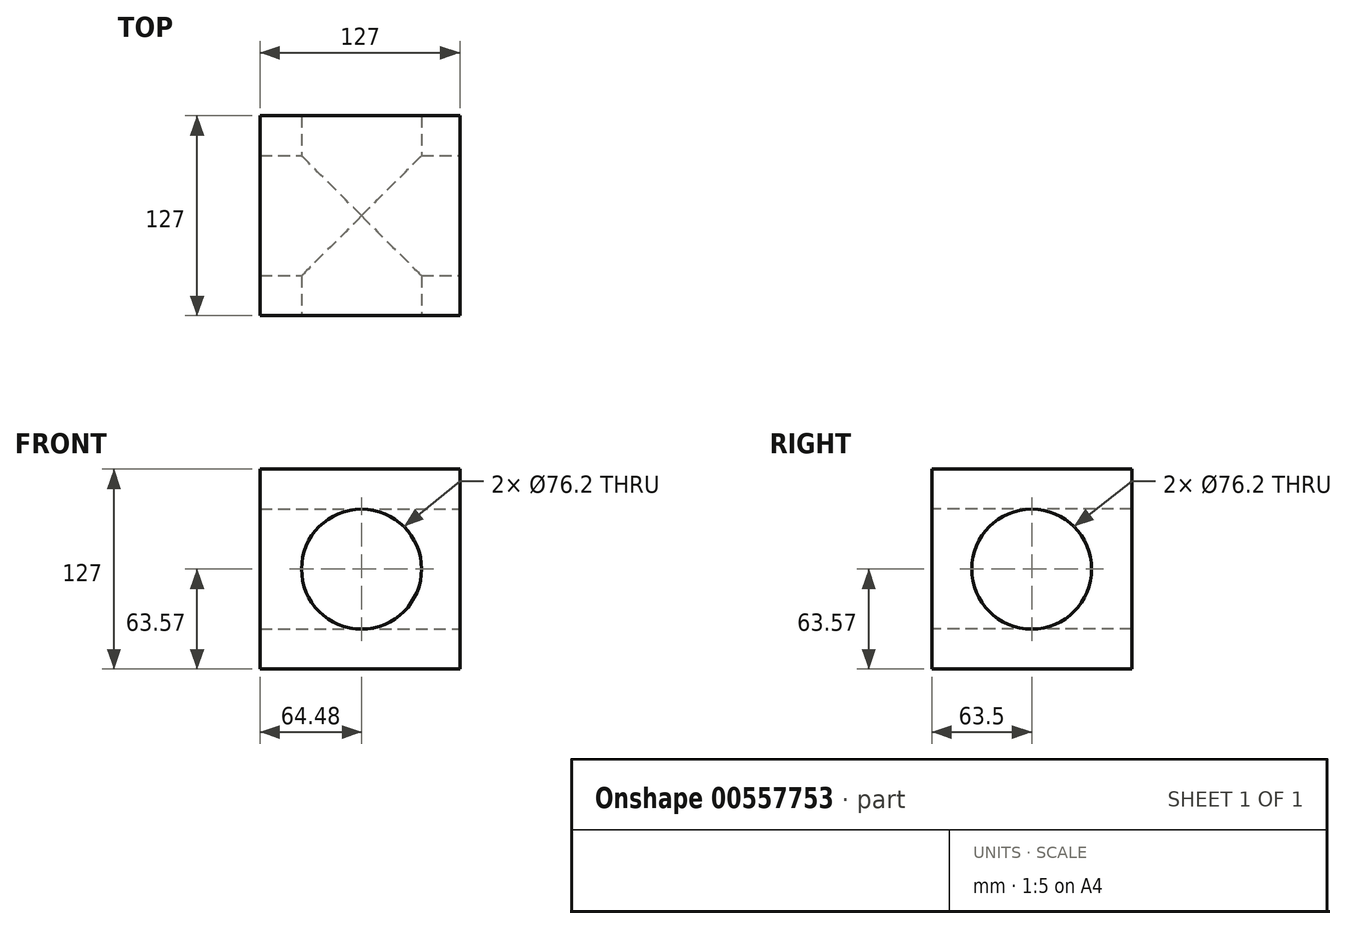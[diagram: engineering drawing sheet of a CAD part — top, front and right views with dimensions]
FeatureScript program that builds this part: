
annotation { "Feature Type Name" : "Feature", "Feature Type Description" : "" }
export const myFeature = defineFeature(function(context is Context, id is Id, definition is map)
    precondition{}
    {
        {
            var Q0;
            Q0=qCreatedBy(makeId("Front.planeOp"),FACE);
            var sketch = newSketch(context, id + "F0", { "sketchPlane" : qUnion([Q0])});
            skLineSegment(sketch, "E0", {"start": v(-64.48, 63.43) * mm, "end": v(-64.48, -63.57) * mm});
            skLineSegment(sketch, "E1", {"start": v(-64.48, -63.57) * mm, "end": v(62.52, -63.57) * mm});
            skLineSegment(sketch, "E2", {"start": v(62.52, -63.57) * mm, "end": v(62.52, 63.43) * mm});
            skLineSegment(sketch, "E3", {"start": v(62.52, 63.43) * mm, "end": v(-64.48, 63.43) * mm});
            skSolve(sketch);
        }
        {
            var Q0;
            Q0 = qSketchRegion(id + "F0", true);
            extrude(context, id + "F1", {"entities" : qUnion([Q0]), "depth" : 127 * mm, "offsetDistance" : 25.4 * mm});
        }
        {
            var Q0;
            Q0=makeQuery(id+"F1.opExtrude","CAP_FACE",FACE,{"disambiguationData":[OSD([sQuery(id+"F0.wireOp",EDGE,"E0"),sQuery(id+"F0.wireOp",EDGE,"E1"),sQuery(id+"F0.wireOp",EDGE,"E2"),sQuery(id+"F0.wireOp",EDGE,"E3")])],"isStart":false});
            var sketch = newSketch(context, id + "F2", { "sketchPlane" : qUnion([Q0])});
            skCircle(sketch, "E4", {"center": v(0, 0) * mm, "radius": 38.1 * mm});
            skSolve(sketch);
        }
        {
            var Q0;
            Q0=makeQuery(id+"F2.imprint","IMPRINT",FACE,{"disambiguationData":[TD([[makeQuery(id+"F2.imprint","IMPRINT",EDGE,{"derivedFrom":sQuery(id+"F2.wireOp",EDGE,"E4")}),1.0]])]});
            extrude(context, id + "F3", {"entities" : qUnion([Q0]), "operationType" : NewBodyOperationType.REMOVE, "endBound" : BoundingType.THROUGH_ALL, "oppositeDirection" : true, "depth" : 127 * mm, "offsetDistance" : 25.4 * mm});
        }
        {
            var Q0;
            Q0=makeQuery(id+"F1.opExtrude","SWEPT_FACE",FACE,{"disambiguationData":[OSD([sQuery(id+"F0.wireOp",EDGE,"E2")])]});
            var sketch = newSketch(context, id + "F4", { "sketchPlane" : qUnion([Q0])});
            skCircle(sketch, "E5", {"center": v(-63.5, 0) * mm, "radius": 38.1 * mm});
            skPoint(sketch, "E5.centerSnap0", {"position": v(-63.5, 63.43) * mm});
            skSolve(sketch);
        }
        {
            var Q0;
            Q0=makeQuery(id+"F4.imprint","IMPRINT",FACE,{"disambiguationData":[TD([[makeQuery(id+"F4.imprint","IMPRINT",EDGE,{"derivedFrom":sQuery(id+"F4.wireOp",EDGE,"E5")}),1.0]])]});
            extrude(context, id + "F5", {"entities" : qUnion([Q0]), "operationType" : NewBodyOperationType.REMOVE, "endBound" : BoundingType.THROUGH_ALL, "oppositeDirection" : true, "depth" : 25.4 * mm, "offsetDistance" : 25.4 * mm});
        }
    });
